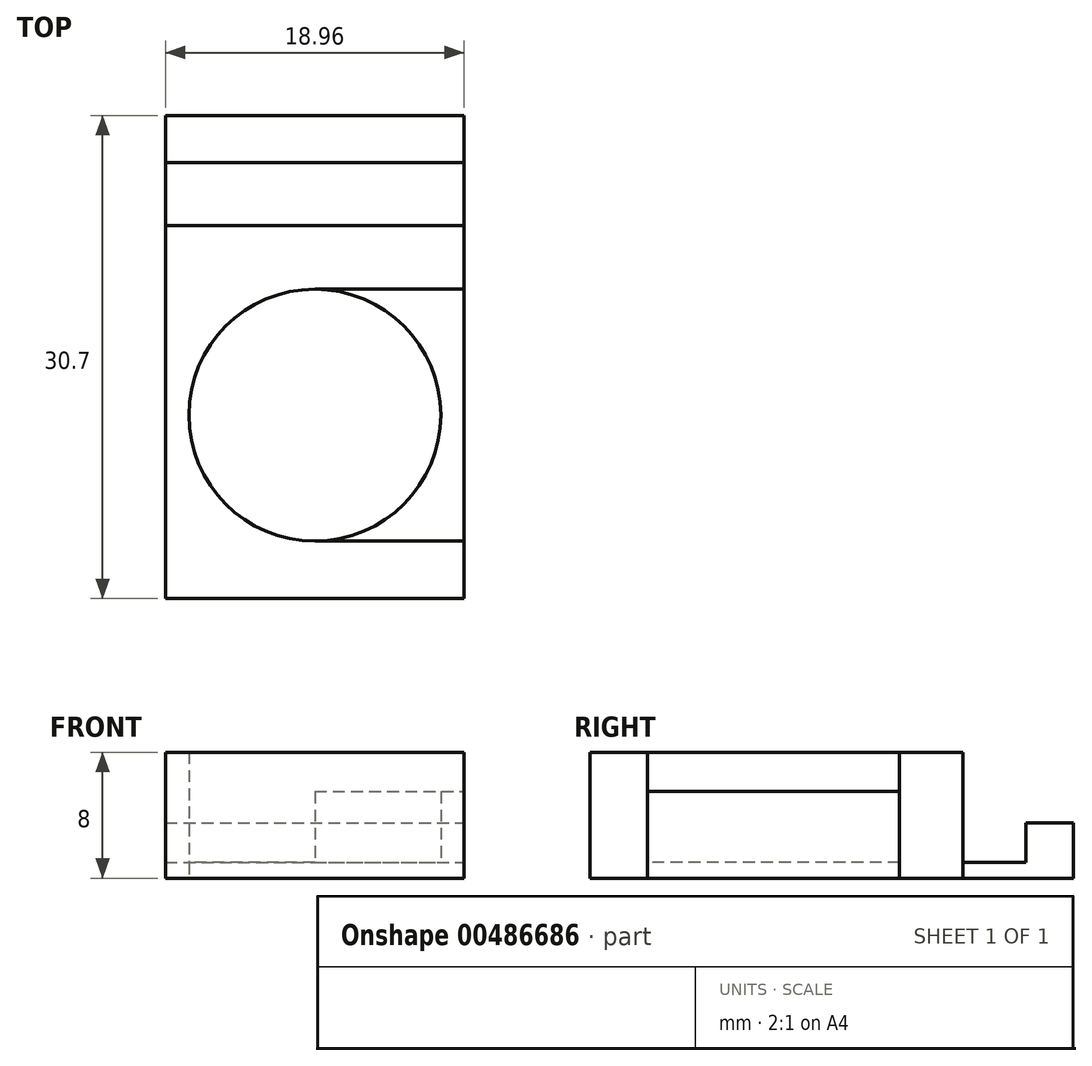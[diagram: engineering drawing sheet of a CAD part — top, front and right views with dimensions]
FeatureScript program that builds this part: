
annotation { "Feature Type Name" : "Feature", "Feature Type Description" : "" }
export const myFeature = defineFeature(function(context is Context, id is Id, definition is map)
    precondition{}
    {
        {
            var Q0;
            Q0=qCreatedBy(makeId("Top.planeOp"),FACE);
            var sketch = newSketch(context, id + "F0", { "sketchPlane" : qUnion([Q0])});
            skLineSegment(sketch, "E0.bottom", {"start": v(9.48, 15.35) * mm, "end": v(-9.48, 15.35) * mm});
            skLineSegment(sketch, "E0.top", {"start": v(9.48, -15.35) * mm, "end": v(-9.48, -15.35) * mm});
            skLineSegment(sketch, "E0.left", {"start": v(9.48, 15.35) * mm, "end": v(9.48, -15.35) * mm});
            skLineSegment(sketch, "E0.right", {"start": v(-9.48, 15.35) * mm, "end": v(-9.48, -15.35) * mm});
            skPoint(sketch, "E0.middle", {"position": v(0, 0) * mm});
            skLineSegment(sketch, "E1.bottom", {"start": v(-9.48, 12.35) * mm, "end": v(9.48, 12.35) * mm});
            skLineSegment(sketch, "E1.top", {"start": v(-9.48, 8.35) * mm, "end": v(9.48, 8.35) * mm});
            skLineSegment(sketch, "E1.left", {"start": v(-9.48, 12.35) * mm, "end": v(-9.48, 8.35) * mm});
            skLineSegment(sketch, "E1.right", {"start": v(9.48, 12.35) * mm, "end": v(9.48, 8.35) * mm});
            skCircle(sketch, "E2", {"center": v(0, -3.69) * mm, "radius": 8 * mm});
            skLineSegment(sketch, "E3.bottom", {"start": v(0, 4.31) * mm, "end": v(9.48, 4.31) * mm});
            skLineSegment(sketch, "E3.top", {"start": v(0, -11.69) * mm, "end": v(9.48, -11.69) * mm});
            skLineSegment(sketch, "E3.left", {"start": v(0, 4.31) * mm, "end": v(0, -11.69) * mm});
            skLineSegment(sketch, "E3.right", {"start": v(9.48, 4.31) * mm, "end": v(9.48, -11.69) * mm});
            skSolve(sketch);
        }
        {
            var Q0;
            {var subQ0=sQuery(id+"F0.wireOp",EDGE,"E3.left");Q0=makeQuery(id+"F0.imprint","IMPRINT",FACE,{"disambiguationData":[TD([[makeQuery(id+"F0.imprint","IMPRINT",EDGE,{"derivedFrom":subQ0}),-1.0]])]});}
            var Q1;
            {var subQ0=sQuery(id+"F0.wireOp",EDGE,"E3.left");Q1=makeQuery(id+"F0.imprint","IMPRINT",FACE,{"disambiguationData":[TD([[makeQuery(id+"F0.imprint","IMPRINT",EDGE,{"derivedFrom":subQ0}),1.0]])]});}
            var Q2;
            Q2=makeQuery(id+"F0.imprint","IMPRINT",FACE,{"disambiguationData":[TD([[makeQuery(id+"F0.imprint","IMPRINT",EDGE,{"derivedFrom":sQuery(id+"F0.wireOp",EDGE,"E1.bottom")}),-1.0]])]});
            extrude(context, id + "F1", {"entities" : qUnion([Q0, Q1, Q2]), "depth" : 1 * mm});
        }
        {
            var Q0;
            {var subQ1=sQuery(id+"F0.wireOp",EDGE,"E3.bottom");Q0=makeQuery(id+"F0.imprint","IMPRINT",FACE,{"disambiguationData":[TD([[makeQuery(id+"F0.imprint","IMPRINT",EDGE,{"derivedFrom":subQ1}),-1.0]])]});}
            extrude(context, id + "F2", {"entities" : qUnion([Q0]), "operationType" : NewBodyOperationType.ADD, "depth" : 5.5 * mm});
        }
        {
            var Q0;
            {var subQ1=sQuery(id+"F0.wireOp",EDGE,"E0.top");Q0=makeQuery(id+"F0.imprint","IMPRINT",FACE,{"disambiguationData":[TD([[makeQuery(id+"F0.imprint","IMPRINT",EDGE,{"derivedFrom":subQ1}),-1.0]])]});}
            extrude(context, id + "F3", {"entities" : qUnion([Q0]), "depth" : 8 * mm});
        }
        {
            var Q0;
            {var subQ0=sQuery(id+"F0.wireOp",EDGE,"E0.bottom");Q0=makeQuery(id+"F0.imprint","IMPRINT",FACE,{"disambiguationData":[TD([[makeQuery(id+"F0.imprint","IMPRINT",EDGE,{"derivedFrom":subQ0}),1.0]])]});}
            extrude(context, id + "F4", {"entities" : qUnion([Q0]), "operationType" : NewBodyOperationType.ADD, "depth" : 3.5 * mm});
        }
    });
